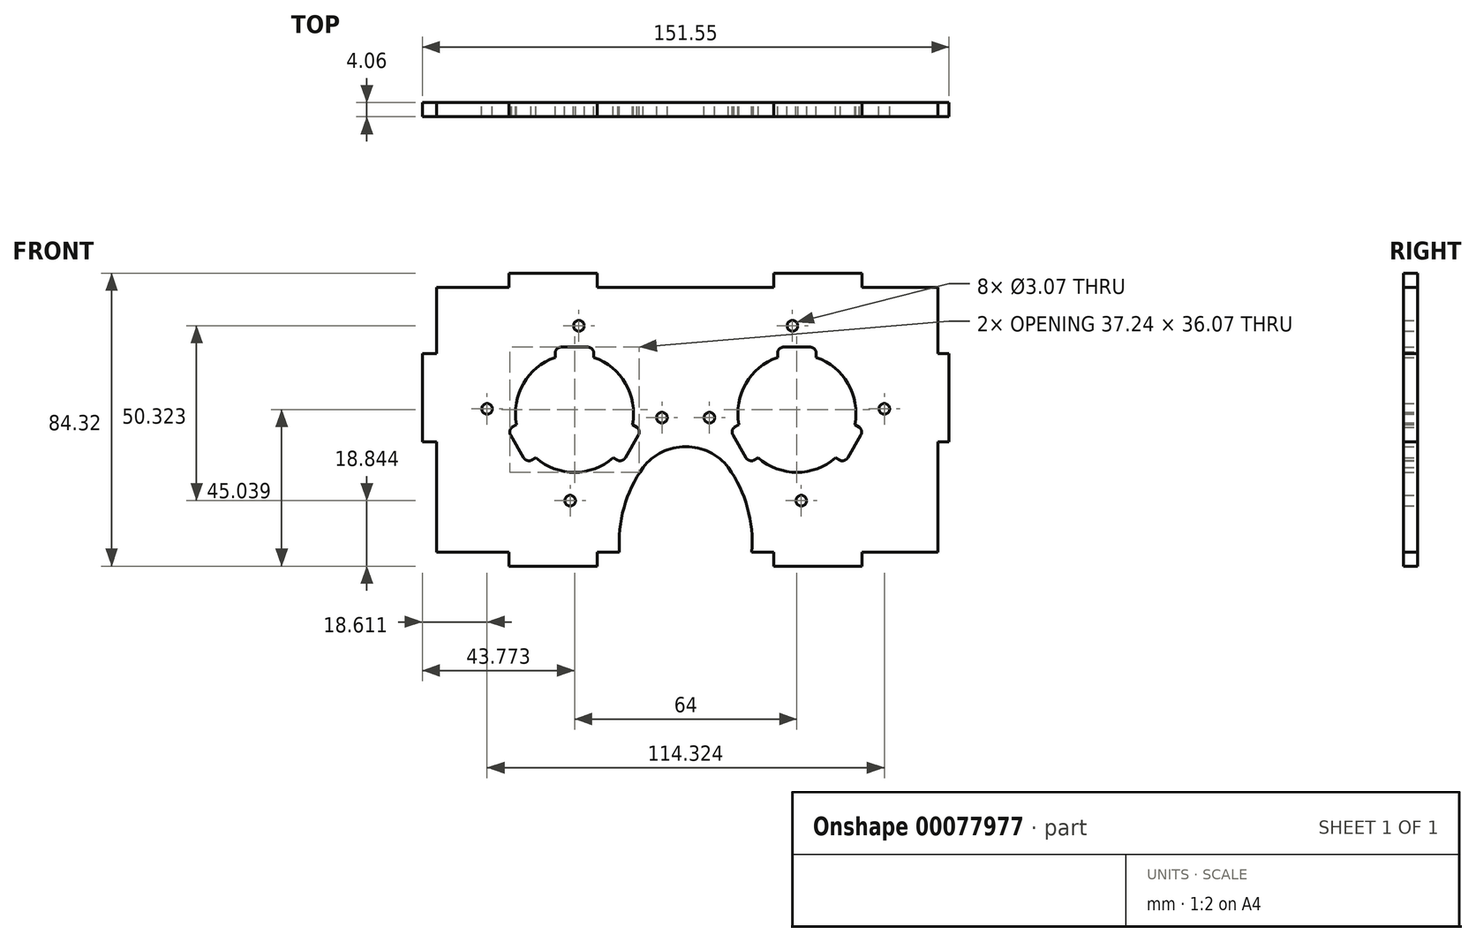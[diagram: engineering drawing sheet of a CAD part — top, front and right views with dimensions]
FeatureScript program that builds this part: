
annotation { "Feature Type Name" : "Feature", "Feature Type Description" : "" }
export const myFeature = defineFeature(function(context is Context, id is Id, definition is map)
    precondition{}
    {
        {
            var Q0;
            Q0=qCreatedBy(makeId("Front.planeOp"),FACE);
            var sketch = newSketch(context, id + "F0", { "sketchPlane" : qUnion([Q0])});
            skLineSegment(sketch, "E0.top", {"start": v(-104.23, 10.4) * mm, "end": v(-83.32, 10.4) * mm});
            skLineSegment(sketch, "E0.right", {"start": v(40.04, 86.6) * mm, "end": v(40.04, 67.55) * mm});
            skLineSegment(sketch, "E1.trimOffspring", {"start": v(-13.04, 10.4) * mm, "end": v(-7.12, 10.4) * mm});
            skPoint(sketch, "E2.orphan", {"position": v(-32.1, 10.4) * mm});
            skPoint(sketch, "E3.endSnap0", {"position": v(-32.1, 60.31) * mm});
            skLineSegment(sketch, "E4", {"start": v(-104.23, 86.6) * mm, "end": v(-83.32, 86.6) * mm});
            skLineSegment(sketch, "E5.top", {"start": v(-83.32, 90.66) * mm, "end": v(-57.92, 90.66) * mm});
            skLineSegment(sketch, "E5.left", {"start": v(-83.32, 86.6) * mm, "end": v(-83.32, 90.66) * mm});
            skLineSegment(sketch, "E5.right", {"start": v(-57.92, 86.6) * mm, "end": v(-57.92, 90.66) * mm});
            skLineSegment(sketch, "E6.top", {"start": v(-7.12, 90.66) * mm, "end": v(18.28, 90.66) * mm});
            skLineSegment(sketch, "E6.left", {"start": v(-7.12, 86.6) * mm, "end": v(-7.12, 90.66) * mm});
            skLineSegment(sketch, "E6.right", {"start": v(18.28, 86.6) * mm, "end": v(18.28, 90.66) * mm});
            skPoint(sketch, "E7.MirrorCS.end.orphan", {"position": v(18.28, 86.6) * mm});
            skLineSegment(sketch, "E8.MirrorCS", {"start": v(-83.32, 10.4) * mm, "end": v(-83.32, 6.34) * mm});
            skLineSegment(sketch, "E9.MirrorCS", {"start": v(-83.32, 6.34) * mm, "end": v(-57.92, 6.34) * mm});
            skLineSegment(sketch, "E10.MirrorCS", {"start": v(-57.92, 10.4) * mm, "end": v(-57.92, 6.34) * mm});
            skLineSegment(sketch, "E11.MirrorCS", {"start": v(-7.12, 10.4) * mm, "end": v(-7.12, 6.34) * mm});
            skLineSegment(sketch, "E12.MirrorCS", {"start": v(-7.12, 6.34) * mm, "end": v(18.28, 6.34) * mm});
            skLineSegment(sketch, "E13.MirrorCS", {"start": v(18.28, 10.4) * mm, "end": v(18.28, 6.34) * mm});
            skLineSegment(sketch, "E14.trimOffspring", {"start": v(-57.92, 10.4) * mm, "end": v(-51.57, 10.4) * mm});
            skLineSegment(sketch, "E15.trimOffspring", {"start": v(18.28, 10.4) * mm, "end": v(40.04, 10.4) * mm});
            skLineSegment(sketch, "E16", {"start": v(18.28, 86.6) * mm, "end": v(40.04, 86.6) * mm});
            skLineSegment(sketch, "E17", {"start": v(-57.92, 86.6) * mm, "end": v(-7.12, 86.6) * mm});
            skLineSegment(sketch, "E18.trimOffspring", {"start": v(-104.23, 34.02) * mm, "end": v(-104.23, 10.4) * mm});
            skLineSegment(sketch, "E19.trimOffspring", {"start": v(40.04, 34.02) * mm, "end": v(40.04, 10.4) * mm});
            skLineSegment(sketch, "E20", {"start": v(-104.23, 86.6) * mm, "end": v(-104.23, 67.55) * mm});
            skLineSegment(sketch, "E21", {"start": v(-104.23, 67.55) * mm, "end": v(-108.93, 67.55) * mm});
            skLineSegment(sketch, "E22", {"start": v(-108.3, 64.22) * mm, "end": v(-108.3, 67.55) * mm});
            skLineSegment(sketch, "E23.bottom", {"start": v(-108.3, 67.55) * mm, "end": v(-104.23, 67.55) * mm});
            skLineSegment(sketch, "E23.top", {"start": v(-108.3, 42.15) * mm, "end": v(-104.23, 42.15) * mm});
            skLineSegment(sketch, "E23.left", {"start": v(-108.3, 67.55) * mm, "end": v(-108.3, 42.15) * mm});
            skLineSegment(sketch, "E24.MirrorCS", {"start": v(43.26, 67.55) * mm, "end": v(39.2, 67.55) * mm});
            skLineSegment(sketch, "E25.MirrorCS", {"start": v(43.26, 67.55) * mm, "end": v(43.26, 42.15) * mm});
            skLineSegment(sketch, "E26.MirrorCS", {"start": v(40.04, 42.15) * mm, "end": v(43.26, 42.15) * mm});
            skLineSegment(sketch, "E27", {"start": v(40.04, 34.02) * mm, "end": v(40.04, 42.15) * mm});
            skPoint(sketch, "E28.orphan", {"position": v(18.28, 42.15) * mm});
            skLineSegment(sketch, "E29.trimOffspring", {"start": v(-104.23, 42.15) * mm, "end": v(-104.23, 34.02) * mm});
            skLineSegment(sketch, "E30", {"start": v(-32.52, 86.6) * mm, "end": v(-32.52, 40.75) * mm});
            skArc(sketch, "E31", {"start": v(-44.8, 34.74) * mm, "mid": v(-50.29, 23.16) * mm, "end": v(-51.57, 10.4) * mm});
            skArc(sketch, "E32.MirrorCS", {"start": v(-20.23, 34.74) * mm, "mid": v(-14.75, 23.16) * mm, "end": v(-13.47, 10.4) * mm});
            skArc(sketch, "E33", {"start": v(-20.23, 34.74) * mm, "mid": v(-32.52, 40.75) * mm, "end": v(-44.8, 34.74) * mm});
            skLineSegment(sketch, "E34.trimOffspring", {"start": v(-13.47, 10.4) * mm, "end": v(-13.04, 10.4) * mm});
            skLineSegment(sketch, "E35", {"start": v(-32.52, 50.35) * mm, "end": v(-64.52, 50.35) * mm});
            skArc(sketch, "E36", {"start": v(-70.07, 66.41) * mm, "mid": v(-79.24, 58.85) * mm, "end": v(-81.2, 47.12) * mm});
            skArc(sketch, "E37.MirrorC", {"start": v(5.04, 66.41) * mm, "mid": v(14.2, 58.85) * mm, "end": v(16.18, 47.12) * mm});
            skArc(sketch, "E38.trimOffspring", {"start": v(-75.65, 37.5) * mm, "mid": v(-64.52, 33.35) * mm, "end": v(-53.38, 37.5) * mm});
            skArc(sketch, "E39.trimOffspring", {"start": v(-47.82, 47.12) * mm, "mid": v(-49.8, 58.85) * mm, "end": v(-58.96, 66.41) * mm});
            skArc(sketch, "E40.trimOffspring", {"start": v(-17.2, 47.12) * mm, "mid": v(-15.24, 58.85) * mm, "end": v(-6.07, 66.41) * mm});
            skArc(sketch, "E41.trimOffspring", {"start": v(10.62, 37.5) * mm, "mid": v(-0.52, 33.35) * mm, "end": v(-11.65, 37.5) * mm});
            skLineSegment(sketch, "E42.MirrorCS", {"start": v(3.19, 69.41) * mm, "end": v(-4.22, 69.41) * mm});
            skArc(sketch, "E43.MirrorCS", {"start": v(-4.22, 69.41) * mm, "mid": v(-5.4, 69) * mm, "end": v(-6.07, 67.97) * mm});
            skLineSegment(sketch, "E44.MirrorCS", {"start": v(-6.07, 67.97) * mm, "end": v(-6.07, 66.41) * mm});
            skLineSegment(sketch, "E45.MirrorCS", {"start": v(5.04, 66.41) * mm, "end": v(5.04, 67.97) * mm});
            skArc(sketch, "E46.MirrorCS", {"start": v(3.19, 69.41) * mm, "mid": v(4.36, 69) * mm, "end": v(5.04, 67.97) * mm});
            skArc(sketch, "E47.MirrorCS", {"start": v(-15.18, 37.6) * mm, "mid": v(-14.24, 36.79) * mm, "end": v(-13, 36.72) * mm});
            skLineSegment(sketch, "E48.MirrorCS", {"start": v(-13, 36.72) * mm, "end": v(-11.65, 37.5) * mm});
            skLineSegment(sketch, "E49.MirrorCS", {"start": v(-18.88, 44.02) * mm, "end": v(-15.18, 37.6) * mm});
            skArc(sketch, "E50.MirrorCS", {"start": v(-18.88, 44.02) * mm, "mid": v(-19.12, 45.24) * mm, "end": v(-18.55, 46.35) * mm});
            skLineSegment(sketch, "E51.MirrorCS", {"start": v(-17.2, 47.12) * mm, "end": v(-18.55, 46.35) * mm});
            skLineSegment(sketch, "E52.MirrorCS", {"start": v(17.52, 46.35) * mm, "end": v(16.18, 47.12) * mm});
            skArc(sketch, "E53.MirrorCS", {"start": v(17.85, 44.02) * mm, "mid": v(18.08, 45.24) * mm, "end": v(17.52, 46.35) * mm});
            skLineSegment(sketch, "E54.MirrorCS", {"start": v(14.14, 37.6) * mm, "end": v(17.85, 44.02) * mm});
            skArc(sketch, "E55.MirrorCS", {"start": v(14.14, 37.6) * mm, "mid": v(13.2, 36.79) * mm, "end": v(11.96, 36.72) * mm});
            skLineSegment(sketch, "E56.MirrorCS", {"start": v(10.62, 37.5) * mm, "end": v(11.96, 36.72) * mm});
            skLineSegment(sketch, "E57.MirrorCS", {"start": v(-68.22, 69.41) * mm, "end": v(-60.81, 69.41) * mm});
            skArc(sketch, "E58.MirrorCS", {"start": v(-60.81, 69.41) * mm, "mid": v(-59.64, 69) * mm, "end": v(-58.96, 67.97) * mm});
            skLineSegment(sketch, "E59.MirrorCS", {"start": v(-58.96, 67.97) * mm, "end": v(-58.96, 66.41) * mm});
            skLineSegment(sketch, "E60.MirrorCS", {"start": v(-70.07, 66.41) * mm, "end": v(-70.07, 67.97) * mm});
            skArc(sketch, "E61.MirrorCS", {"start": v(-68.22, 69.41) * mm, "mid": v(-69.4, 69) * mm, "end": v(-70.07, 67.97) * mm});
            skLineSegment(sketch, "E62.MirrorCS", {"start": v(-82.55, 46.35) * mm, "end": v(-81.2, 47.12) * mm});
            skArc(sketch, "E63.MirrorCS", {"start": v(-82.88, 44.02) * mm, "mid": v(-83.12, 45.24) * mm, "end": v(-82.55, 46.35) * mm});
            skLineSegment(sketch, "E64.MirrorCS", {"start": v(-79.18, 37.6) * mm, "end": v(-82.88, 44.02) * mm});
            skArc(sketch, "E65.MirrorCS", {"start": v(-79.18, 37.6) * mm, "mid": v(-78.24, 36.79) * mm, "end": v(-77, 36.72) * mm});
            skLineSegment(sketch, "E66.MirrorCS", {"start": v(-75.65, 37.5) * mm, "end": v(-77, 36.72) * mm});
            skLineSegment(sketch, "E67.MirrorCS", {"start": v(-52.04, 36.72) * mm, "end": v(-53.38, 37.5) * mm});
            skArc(sketch, "E68.MirrorCS", {"start": v(-49.86, 37.6) * mm, "mid": v(-50.8, 36.79) * mm, "end": v(-52.04, 36.72) * mm});
            skLineSegment(sketch, "E69.MirrorCS", {"start": v(-46.15, 44.02) * mm, "end": v(-49.86, 37.6) * mm});
            skArc(sketch, "E70.MirrorCS", {"start": v(-46.15, 44.02) * mm, "mid": v(-45.92, 45.24) * mm, "end": v(-46.48, 46.35) * mm});
            skLineSegment(sketch, "E71.MirrorCS", {"start": v(-47.82, 47.12) * mm, "end": v(-46.48, 46.35) * mm});
            skLineSegment(sketch, "E72", {"start": v(-1.78, 73.17) * mm, "end": v(-1.78, 75.5) * mm});
            skCircle(sketch, "E73", {"center": v(-1.78, 75.5) * mm, "radius": 1.54 * mm});
            skCircle(sketch, "E74.1.0", {"center": v(-25.68, 49.08) * mm, "radius": 1.54 * mm});
            skCircle(sketch, "E74.2.0", {"center": v(0.75, 25.18) * mm, "radius": 1.54 * mm});
            skCircle(sketch, "E74.3.0", {"center": v(24.64, 51.61) * mm, "radius": 1.54 * mm});
            skCircle(sketch, "E75.MirrorC", {"center": v(-63.25, 75.5) * mm, "radius": 1.54 * mm});
            skCircle(sketch, "E76.MirrorC", {"center": v(-39.36, 49.08) * mm, "radius": 1.54 * mm});
            skCircle(sketch, "E77.MirrorC", {"center": v(-89.68, 51.61) * mm, "radius": 1.54 * mm});
            skCircle(sketch, "E78.MirrorC", {"center": v(-65.78, 25.18) * mm, "radius": 1.54 * mm});
            skSolve(sketch);
        }
        {
            var Q0;
            Q0=makeQuery(id+"F0.imprint","IMPRINT",FACE,{"disambiguationData":[TD([[makeQuery(id+"F0.imprint","IMPRINT",EDGE,{"derivedFrom":sQuery(id+"F0.wireOp",EDGE,"E0.top")}),1.0]])]});
            var Q1;
            {var subQ2=sQuery(id+"F0.wireOp",EDGE,"E0.right");Q1=makeQuery(id+"F0.imprint","IMPRINT",FACE,{"disambiguationData":[TD([[makeQuery(id+"F0.imprint","IMPRINT",EDGE,{"derivedFrom":subQ2}),-1.0]])]});}
            extrude(context, id + "F1", {"entities" : qUnion([Q0, Q1]), "depth" : 4.06 * mm});
        }
    });
